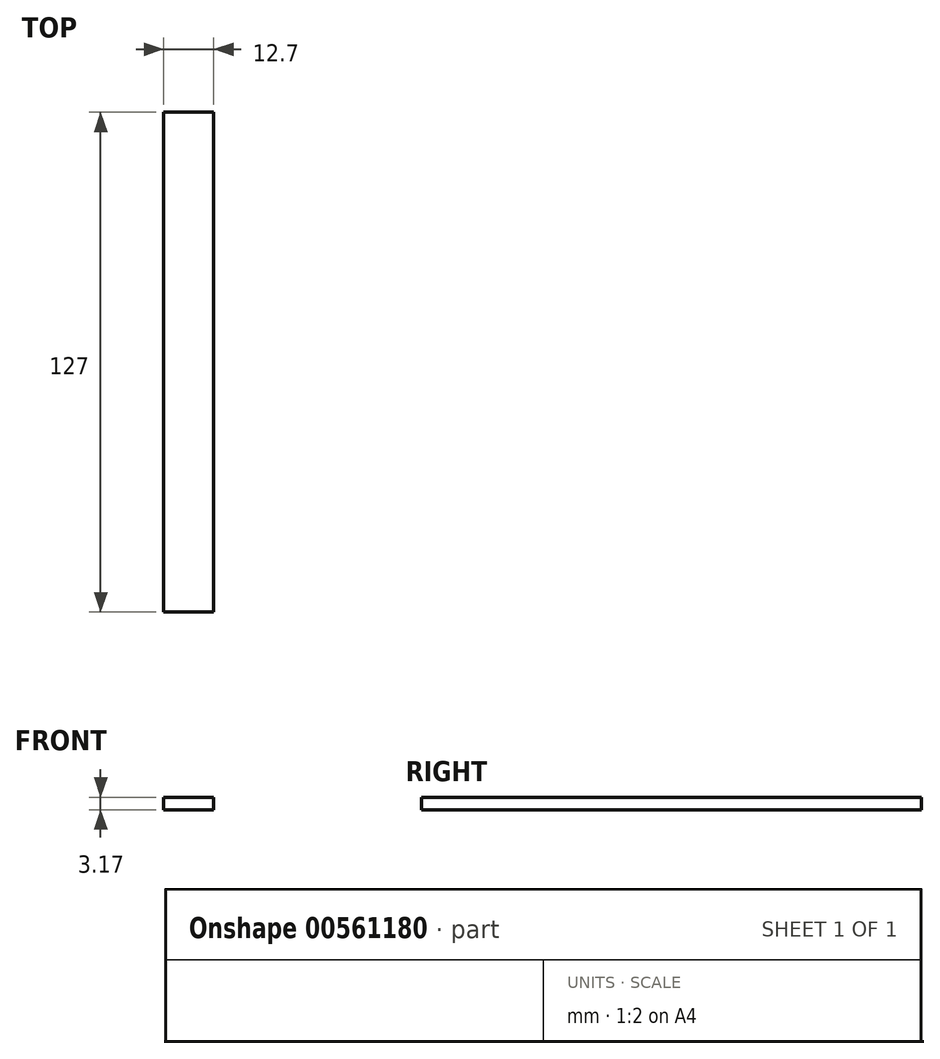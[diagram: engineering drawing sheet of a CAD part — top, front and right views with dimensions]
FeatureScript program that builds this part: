
annotation { "Feature Type Name" : "Feature", "Feature Type Description" : "" }
export const myFeature = defineFeature(function(context is Context, id is Id, definition is map)
    precondition{}
    {
        {
            var Q0;
            Q0=qCreatedBy(makeId("Top.planeOp"),FACE);
            var sketch = newSketch(context, id + "F0", { "sketchPlane" : qUnion([Q0])});
            skLineSegment(sketch, "E0.bottom", {"start": v(0, 0) * mm, "end": v(-12.7, 0) * mm});
            skLineSegment(sketch, "E0.top", {"start": v(0, 127) * mm, "end": v(-12.7, 127) * mm});
            skLineSegment(sketch, "E0.left", {"start": v(0, 0) * mm, "end": v(0, 127) * mm});
            skLineSegment(sketch, "E0.right", {"start": v(-12.7, 0) * mm, "end": v(-12.7, 127) * mm});
            skSolve(sketch);
        }
        {
            var Q0;
            Q0=makeQuery(id+"F0.imprint","IMPRINT",FACE,{"disambiguationData":[TD([[makeQuery(id+"F0.imprint","IMPRINT",EDGE,{"derivedFrom":sQuery(id+"F0.wireOp",EDGE,"E0.bottom")}),-1.0]])]});
            extrude(context, id + "F1", {"entities" : qUnion([Q0]), "depth" : 3.17 * mm, "offsetDistance" : 25.4 * mm});
        }
    });
